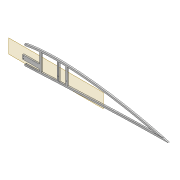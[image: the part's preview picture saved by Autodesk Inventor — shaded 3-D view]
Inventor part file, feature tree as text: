
AUTODESK INVENTOR PART (.ipt)
format: ipt  version: 2022 (Build 260153000, 153)  size: 449,536 bytes
history: native  units: mm
features: extrude x8, sketch x7, projected_geometry x6, fillet x2, shell x1, plane x1
ambient origin geometry x8: Origin, YZ Plane, XZ Plane, XY Plane, X Axis, Y Axis, Z Axis, Center Point
bodies: Solid1 (feature_tree)
feature tree (25):
  extrude  "Extrusion1"  Depth=5.0mm
  shell  "Shell1"  Thickness=2.0mm
  extrude  "Extrusion8"  Depth=5.9mm
  extrude  "Extrusion3"  Depth=10.0mm TaperAngle=0.0deg
  extrude  "Extrusion4"  Depth=2.0mm
  fillet  "Fillet1"  Radius=5.0mm
  sketch  "Sketch10"  dims[d22=4.0mm d23=0.0mm d31=2.0mm d32=5.0mm]
  extrude  "Extrusion5"  Depth=2.5mm
  plane  "Work Plane2"
  extrude  "Extrusion9"  Depth=1.6mm
  fillet  "Fillet2"  Radius=2.5mm
  extrude  "Extrusion10"  Depth=0.5mm
  extrude  "Extrusion11"  Depth=0.5mm TaperAngle=0.0deg
  sketch  "Sketch3"  dims[d0=4.0mm d1=0.0mm d2=5.0mm d7=2.0mm]
  sketch  "Sketch8"  dims[d8=2.0mm d9=5.9mm]
  sketch  "Sketch9"  dims[d13=10.0mm d14=0.0mm d16=10.0mm d17=0.0mm]
  projected_geometry  "Projected Loop4"
  projected_geometry  "Projected Loop10"
  sketch  "Sketch24"  dims[d34=1.6mm d35=2.5mm]
  projected_geometry  "Projected Loop11"
  projected_geometry  "Projected Loop12"
  projected_geometry  "Projected Loop13"
  sketch  "Sketch26"  dims[d37=5.0mm d38=1.6mm d40=2.5mm]
  projected_geometry  "Projected Loop14"
  sketch  "Sketch27"  dims[d62=80.0mm d63=6.0mm d64=4.0mm d65=0.0mm d66=3.0mm d67=12.0mm d68=5.0mm d69=50.0mm d70=12.0mm d71=3.05mm d72=10.0mm d73=0.0mm d74=2.0mm d75=100.0mm d76=20.0mm d77=0.5mm d78=10.0mm d79=0.0mm d80=10.0mm d81=0.0mm]
